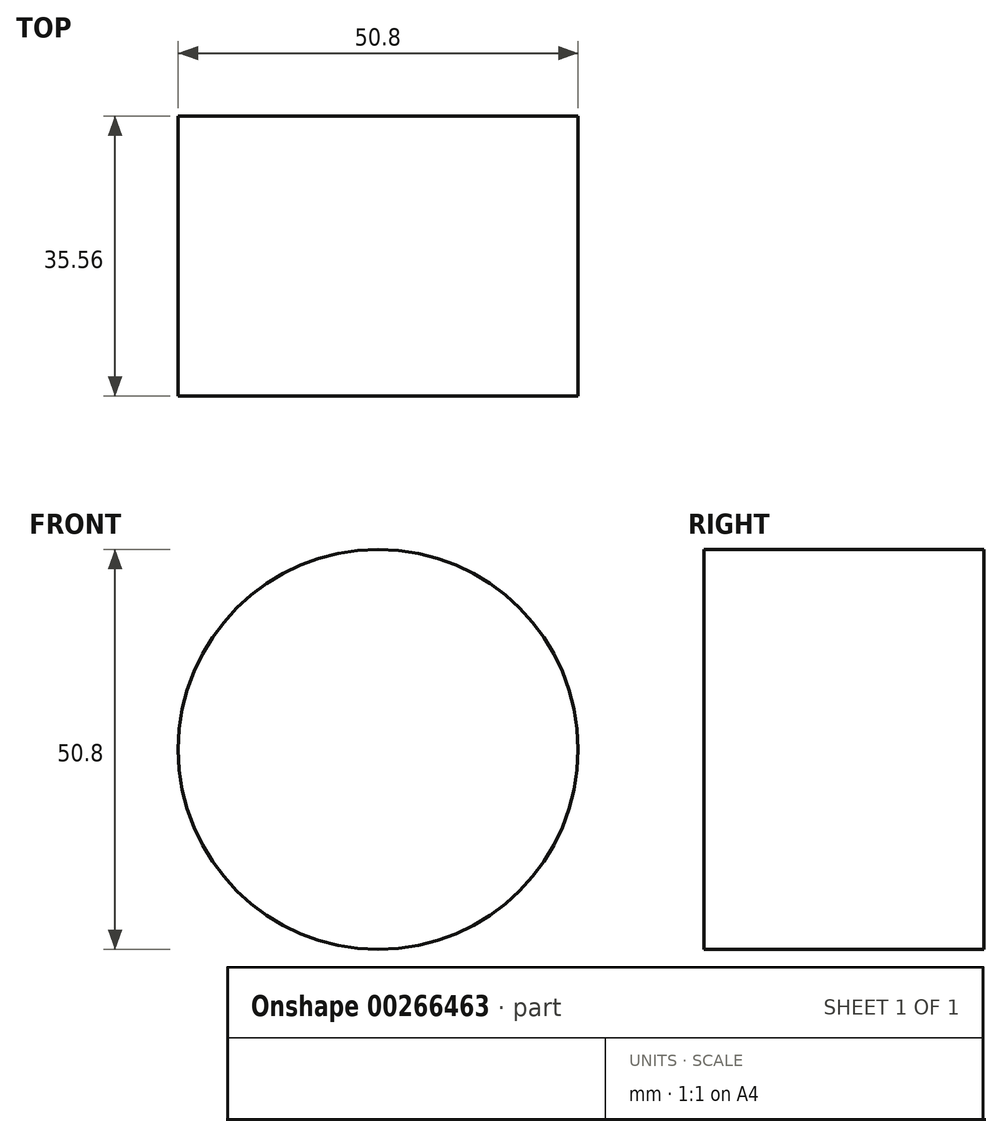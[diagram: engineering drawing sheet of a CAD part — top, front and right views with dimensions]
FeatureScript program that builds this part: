
annotation { "Feature Type Name" : "Feature", "Feature Type Description" : "" }
export const myFeature = defineFeature(function(context is Context, id is Id, definition is map)
    precondition{}
    {
        {
            var Q0;
            Q0=qCreatedBy(makeId("Front.planeOp"),FACE);
            var sketch = newSketch(context, id + "F0", { "sketchPlane" : qUnion([Q0])});
            skCircle(sketch, "E0", {"center": v(0, 0) * mm, "radius": 25.4 * mm});
            skSolve(sketch);
        }
        {
            var Q0;
            Q0=makeQuery(id+"F0.imprint","IMPRINT",FACE,{"disambiguationData":[TD([[makeQuery(id+"F0.imprint","IMPRINT",EDGE,{"derivedFrom":sQuery(id+"F0.wireOp",EDGE,"E0")}),1.0]])]});
            extrude(context, id + "F1", {"entities" : qUnion([Q0]), "depth" : 25.4 * mm});
        }
        {
            var Q0;
            Q0=makeQuery(id+"F0.imprint","IMPRINT",FACE,{"disambiguationData":[TD([[makeQuery(id+"F0.imprint","IMPRINT",EDGE,{"derivedFrom":sQuery(id+"F0.wireOp",EDGE,"E0")}),1.0]])]});
            extrude(context, id + "F2", {"entities" : qUnion([Q0]), "operationType" : NewBodyOperationType.ADD, "depth" : 35.56 * mm});
        }
    });
